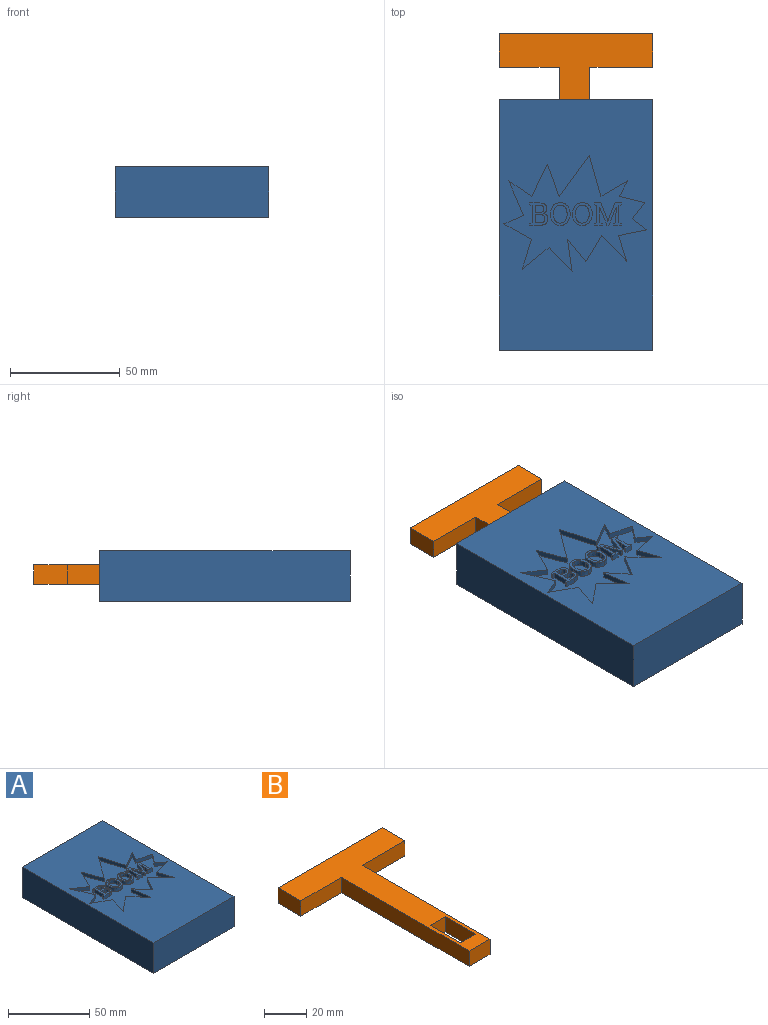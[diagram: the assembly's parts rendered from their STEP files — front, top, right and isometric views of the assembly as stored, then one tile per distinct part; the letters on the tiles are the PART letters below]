
ASSEMBLY  parts=2 mates=1
PART A: 160 faces, bbox 69.9x114.3x22.9 mm
  f0: plane 114.3x69.85mm, normal (0,0,1), area 6341.6mm2, adj f18,f19,f20,f23,f91,f92,f93,f94
  f1: plane 25.4x15.24mm, normal (0,0,1), area 316mm2, adj f3,f4,f5,f9,f10,f11,f12,f24
  f2: plane 25.4x15.24mm, normal (0,0,1), area 316mm2, adj f6,f7,f8,f14,f15,f16,f17,f21
  f3: plane 5.08x4.78mm, normal (0,-1,0), area 24.3mm2, adj f1,f4,f24,f25
  f4: plane 5.08x5.08mm, normal (-1,0,0), area 25.8mm2, adj f1,f3,f5,f25
  f5: cylinder r=3.97mm len=7.94mm, axis (0,0,-1), area 100.6mm2, adj f1,f4,f24,f25
  f6: plane 5.08x5.08mm, normal (-1,0,0), area 25.8mm2, adj f2,f7,f21,f25
  f7: cylinder r=3.97mm len=7.94mm, axis (0,0,-1), area 100.6mm2, adj f2,f6,f8,f25
  f8: plane 5.08x5.08mm, normal (1,0,0), area 25.8mm2, adj f2,f7,f21,f25
  f9: plane 25.4x5.08mm, normal (-1,0,0), area 129mm2, adj f1,f10,f12,f25
  f10: plane 15.24x5.08mm, normal (0,-1,0), area 77.4mm2, adj f1,f9,f11,f25
  f11: plane 25.4x5.08mm, normal (1,0,0), area 129mm2, adj f1,f10,f12,f25
  f12: plane 49.53x17.78mm, normal (0,-1,0), area 648.4mm2, adj f1,f9,f11,f13,f22,f25,f26,f27
  f13: plane 93.98x17.78mm, normal (-1,0,0), area 1671mm2, adj f12,f17,f25,f26
  f14: plane 25.4x5.08mm, normal (1,0,0), area 129mm2, adj f2,f15,f17,f25
  f15: plane 15.24x5.08mm, normal (0,1,0), area 77.4mm2, adj f2,f14,f16,f25
  f16: plane 25.4x5.08mm, normal (-1,0,0), area 129mm2, adj f2,f15,f17,f25
  f17: plane 49.53x17.78mm, normal (0,1,0), area 803.2mm2, adj f2,f13,f14,f16,f22,f25,f26
  f18: plane 114.3x22.86mm, normal (-1,0,0), area 2612.9mm2, adj f0,f19,f23,f25
  f19: plane 69.85x22.86mm, normal (0,-1,0), area 1596.8mm2, adj f0,f18,f20,f25
  f20: plane 114.3x22.86mm, normal (1,0,0), area 2612.9mm2, adj f0,f19,f23,f25
  f21: plane 5.08x4.78mm, normal (0,-1,0), area 24.3mm2, adj f2,f6,f8,f25
  f22: plane 93.98x17.78mm, normal (1,0,0), area 1671mm2, adj f12,f17,f25,f26
  f23: plane 69.85x22.86mm, normal (0,1,0), area 1441.9mm2, adj f0,f18,f20,f25,f26,f27,f28,f29
  f24: plane 5.08x5.08mm, normal (1,0,0), area 25.8mm2, adj f1,f3,f5,f25
  f25: plane 114.3x69.85mm, normal (0,0,-1), area 3960.9mm2, adj f3,f4,f5,f6,f7,f8,f9,f10
  f26: plane 104.14x49.53mm, normal (0,0,-1), area 4809.7mm2, adj f12,f13,f17,f22,f23,f27,f29
  f27: plane 10.16x10.16mm, normal (-1,0,0), area 103.2mm2, adj f12,f23,f26,f28
  f28: plane 15.24x10.16mm, normal (0,0,1), area 154.8mm2, adj f12,f23,f27,f29
  f29: plane 10.16x10.16mm, normal (1,0,0), area 103.2mm2, adj f12,f23,f26,f28
  f30: plane 2.94x2.54mm, normal (-1,0,0), area 7.5mm2, adj f31,f116,f117,f121
  f31: plane 4.11x2.54mm, normal (-1,0.03,0), area 10.4mm2, adj f30,f32,f117,f121
  f32: plane 2.54x0.04mm, normal (-0.18,-0.98,0), area 0.1mm2, adj f31,f33,f117,f121
  f33: plane 8.13x3.28mm, normal (0.93,-0.37,0), area 22.3mm2, adj f32,f34,f117,f121
  f34: plane 2.54x0.91mm, normal (0,-1,0), area 2.3mm2, adj f33,f35,f117,f121
  f35: plane 8.13x3.28mm, normal (-0.93,-0.37,0), area 22.3mm2, adj f34,f36,f117,f121
  f36: plane 2.54x0.04mm, normal (0.18,-0.98,0), area 0.1mm2, adj f35,f37,f117,f121
  f37: plane 4.11x2.54mm, normal (1,0.03,0), area 10.4mm2, adj f36,f38,f117,f121
  f38: plane 2.94x2.54mm, normal (1,0,0), area 7.5mm2, adj f37,f39,f117,f121
  f39: plane 2.54x1.14mm, normal (0.17,0.99,0), area 2.9mm2, adj f38,f40,f117,f121
  f40: plane 2.54x0.88mm, normal (1,0,0), area 2.2mm2, adj f39,f41,f117,f121
  f41: plane 3.64x2.54mm, normal (0,-1,0), area 9.3mm2, adj f40,f42,f117,f121
  f42: plane 2.54x0.88mm, normal (-1,0,0), area 2.2mm2, adj f41,f43,f117,f121
  f43: plane 2.54x1.14mm, normal (-0.17,0.99,0), area 2.9mm2, adj f42,f44,f117,f121
  f44: plane 7.99x2.54mm, normal (-1,0,0), area 20.3mm2, adj f43,f45,f117,f121
  f45: plane 2.54x1.14mm, normal (-0.17,-0.99,0), area 2.9mm2, adj f44,f46,f117,f121
  f46: plane 2.54x0.89mm, normal (-1,0,0), area 2.2mm2, adj f45,f47,f117,f121
  f47: plane 2.89x2.54mm, normal (0,1,0), area 7.3mm2, adj f46,f48,f117,f121
  f48: plane 8.24x3.23mm, normal (0.93,0.37,0), area 22.5mm2, adj f47,f49,f117,f121
  f49: plane 2.54x0.04mm, normal (0,1,0), area 0.1mm2, adj f48,f50,f117,f121
  f50: plane 8.24x3.22mm, normal (-0.93,0.36,0), area 22.5mm2, adj f49,f51,f117,f121
  f51: plane 2.9x2.54mm, normal (0,1,0), area 7.4mm2, adj f50,f52,f117,f121
  f52: plane 2.54x0.89mm, normal (1,0,0), area 2.2mm2, adj f51,f53,f117,f121
  f53: plane 2.54x1.14mm, normal (0.17,-0.99,0), area 2.9mm2, adj f52,f54,f117,f121
  f54: plane 7.99x2.54mm, normal (1,0,0), area 20.3mm2, adj f53,f55,f117,f121
  f55: plane 2.54x1.14mm, normal (0.17,0.99,0), area 2.9mm2, adj f54,f56,f117,f121
  f56: plane 2.54x0.88mm, normal (1,0,0), area 2.2mm2, adj f55,f57,f117,f121
  f57: plane 3.64x2.54mm, normal (0,-1,0), area 9.3mm2, adj f56,f58,f117,f121
  f58: plane 2.54x0.88mm, normal (-1,0,0), area 2.2mm2, adj f57,f116,f117,f121
  f59: extruded ~3.68x2.54mm, area 10.1mm2, adj f60,f112,f117,f120
  f60: plane 2.54x0.15mm, normal (1,0,0), area 0.4mm2, adj f59,f61,f117,f120
  f61: extruded ~3.68x2.54mm, area 10.1mm2, adj f60,f62,f117,f120
  f62: extruded ~3.29x2.54mm, area 9.5mm2, adj f61,f63,f117,f120
  f63: extruded ~3.19x2.54mm, area 9.2mm2, adj f62,f64,f117,f120
  f64: extruded ~3.68x2.54mm, area 10.1mm2, adj f63,f65,f117,f120
  f65: plane 2.54x0.15mm, normal (-1,0,0), area 0.4mm2, adj f64,f66,f117,f120
  f66: extruded ~3.68x2.54mm, area 10.1mm2, adj f65,f67,f117,f120
  f67: extruded ~3.19x2.54mm, area 9.2mm2, adj f66,f112,f117,f120
  f68: extruded ~3.68x2.54mm, area 10.1mm2, adj f69,f113,f117,f119
  f69: plane 2.54x0.15mm, normal (1,0,0), area 0.4mm2, adj f68,f70,f117,f119
  f70: extruded ~3.68x2.54mm, area 10.1mm2, adj f69,f71,f117,f119
  f71: extruded ~3.29x2.54mm, area 9.5mm2, adj f70,f72,f117,f119
  f72: extruded ~3.19x2.54mm, area 9.2mm2, adj f71,f73,f117,f119
  f73: extruded ~3.68x2.54mm, area 10.1mm2, adj f72,f74,f117,f119
  f74: plane 2.54x0.15mm, normal (-1,0,0), area 0.4mm2, adj f73,f75,f117,f119
  f75: extruded ~3.68x2.54mm, area 10.1mm2, adj f74,f76,f117,f119
  f76: extruded ~3.19x2.54mm, area 9.2mm2, adj f75,f113,f117,f119
  f77: plane 4.45x2.54mm, normal (0,1,0), area 11.3mm2, adj f78,f114,f117,f118
  f78: extruded ~2.54x2.48mm, area 6.7mm2, adj f77,f79,f117,f118
  f79: extruded ~2.54x2.06mm, area 5.9mm2, adj f78,f80,f117,f118
  f80: extruded ~2.54x1.21mm, area 3.3mm2, adj f79,f81,f117,f118
  f81: extruded ~2.54x1.13mm, area 3.6mm2, adj f80,f82,f117,f118
  f82: extruded ~2.54x1.44mm, area 4.4mm2, adj f81,f83,f117,f118
  f83: extruded ~2.54x1.64mm, area 4.5mm2, adj f82,f84,f117,f118
  f84: extruded ~2.54x2.13mm, area 6.1mm2, adj f83,f85,f117,f118
  f85: extruded ~2.54x2.45mm, area 6.6mm2, adj f84,f86,f117,f118
  f86: plane 4.88x2.54mm, normal (0,-1,0), area 12.4mm2, adj f85,f87,f117,f118
  f87: plane 2.54x0.88mm, normal (-1,0,0), area 2.2mm2, adj f86,f88,f117,f118
  f88: plane 2.54x1.14mm, normal (-0.17,0.99,0), area 2.9mm2, adj f87,f89,f117,f118
  f89: plane 7.99x2.54mm, normal (-1,0,0), area 20.3mm2, adj f88,f90,f117,f118
  f90: plane 2.54x1.14mm, normal (-0.17,-0.99,0), area 2.9mm2, adj f89,f114,f117,f118
  f91: plane 11.08x10.5mm, normal (0.73,0.69,0), area 38.8mm2, adj f0,f92,f115,f117
  f92: plane 14.68x2.54mm, normal (-0.99,-0.14,0), area 37.7mm2, adj f0,f91,f93,f117
  f93: plane 10.09x8.4mm, normal (0.77,0.64,0), area 33.4mm2, adj f0,f92,f94,f117
  f94: plane 12.03x7.26mm, normal (-0.86,0.52,0), area 35.7mm2, adj f0,f93,f95,f117
  f95: plane 12.03x11.46mm, normal (0.72,0.69,0), area 42.2mm2, adj f0,f94,f96,f117
  f96: plane 11.84x3.82mm, normal (-0.95,-0.31,0), area 31.6mm2, adj f0,f95,f97,f117
  f97: plane 12.83x2.58mm, normal (-0.2,0.98,0), area 33.2mm2, adj f0,f96,f98,f117
  f98: plane 6.53x5.06mm, normal (-0.61,-0.79,0), area 21mm2, adj f0,f97,f99,f117
  f99: plane 7.4x5.73mm, normal (-0.79,0.61,0), area 23.8mm2, adj f0,f98,f100,f117
  f100: plane 11.65x2.92mm, normal (-0.24,-0.97,0), area 30.5mm2, adj f0,f99,f101,f117
  f101: plane 7.04x3.82mm, normal (-0.88,0.48,0), area 20.3mm2, adj f0,f100,f102,f117
  f102: plane 12.22x7.04mm, normal (0.5,-0.87,0), area 35.8mm2, adj f0,f101,f103,f117
  f103: plane 18.71x5.35mm, normal (-0.96,-0.27,0), area 49.4mm2, adj f0,f102,f104,f117
  f104: plane 18.71x13.75mm, normal (0.81,-0.59,0), area 59mm2, adj f0,f103,f105,f117
  f105: plane 14.51x5.35mm, normal (-0.94,-0.35,0), area 39.3mm2, adj f0,f104,f106,f117
  f106: plane 14.51x7.26mm, normal (0.89,-0.45,0), area 41.2mm2, adj f0,f105,f107,f117
  f107: plane 10.36x7.04mm, normal (-0.56,-0.83,0), area 31.8mm2, adj f0,f106,f108,f117
  f108: plane 15.82x6.73mm, normal (0.92,0.39,0), area 43.7mm2, adj f0,f107,f109,f117
  f109: plane 8.98x3.82mm, normal (0.39,-0.92,0), area 24.8mm2, adj f0,f108,f110,f117
  f110: plane 12.6x7.09mm, normal (0.49,0.87,0), area 36.7mm2, adj f0,f109,f111,f117
  f111: plane 13.53x4.2mm, normal (0.96,-0.3,0), area 36mm2, adj f0,f110,f115,f117
  f112: extruded ~3.29x2.54mm, area 9.5mm2, adj f59,f67,f117,f120
  f113: extruded ~3.29x2.54mm, area 9.5mm2, adj f68,f76,f117,f119
  f114: plane 2.54x0.89mm, normal (-1,0,0), area 2.2mm2, adj f77,f90,f117,f118
  f115: plane 12.22x9.93mm, normal (-0.63,0.78,0), area 40mm2, adj f0,f91,f111,f117
  f116: plane 2.54x1.14mm, normal (-0.17,0.99,0), area 2.9mm2, adj f30,f58,f117,f121
  f117: plane 65.15x53.09mm, normal (0,0,1), area 1369mm2, adj f30,f31,f32,f33,f34,f35,f36,f37
  f118: plane 10.15x8.24mm, normal (0,0,1), area 40.4mm2, adj f77,f78,f79,f80,f81,f82,f83,f84
  f119: plane 10.44x8.98mm, normal (0,0,1), area 33.7mm2, adj f68,f69,f70,f71,f72,f73,f74,f75
  f120: plane 10.44x8.98mm, normal (0,0,1), area 33.7mm2, adj f59,f60,f61,f62,f63,f64,f65,f66
  f121: plane 12.29x10.15mm, normal (0,0,1), area 55.8mm2, adj f30,f31,f32,f33,f34,f35,f36,f37
  f122: extruded ~2.91x2.54mm, area 7.8mm2, adj f120,f123,f131,f132
  f123: plane 2.54x0.16mm, normal (-1,0,0), area 0.4mm2, adj f120,f122,f124,f132
  f124: extruded ~2.89x2.54mm, area 7.8mm2, adj f120,f123,f125,f132
  f125: extruded ~2.54x2.34mm, area 6.9mm2, adj f120,f124,f126,f132
  f126: extruded ~2.54x2.24mm, area 6.6mm2, adj f120,f125,f127,f132
  f127: extruded ~2.88x2.54mm, area 7.7mm2, adj f120,f126,f128,f132
  f128: plane 2.54x0.16mm, normal (1,0,0), area 0.4mm2, adj f120,f127,f129,f132
  f129: extruded ~2.9x2.54mm, area 7.8mm2, adj f120,f128,f130,f132
  f130: extruded ~2.54x2.24mm, area 6.6mm2, adj f120,f129,f131,f132
  f131: extruded ~2.54x2.35mm, area 6.9mm2, adj f120,f122,f130,f132
  f132: plane 8.19x6.23mm, normal (0,0,1), area 41.6mm2, adj f122,f123,f124,f125,f126,f127,f128,f129
  f133: extruded ~2.91x2.54mm, area 7.8mm2, adj f119,f134,f142,f143
  f134: plane 2.54x0.16mm, normal (-1,0,0), area 0.4mm2, adj f119,f133,f135,f143
  f135: extruded ~2.89x2.54mm, area 7.8mm2, adj f119,f134,f136,f143
  f136: extruded ~2.54x2.34mm, area 6.9mm2, adj f119,f135,f137,f143
  f137: extruded ~2.54x2.24mm, area 6.6mm2, adj f119,f136,f138,f143
  f138: extruded ~2.88x2.54mm, area 7.7mm2, adj f119,f137,f139,f143
  f139: plane 2.54x0.16mm, normal (1,0,0), area 0.4mm2, adj f119,f138,f140,f143
  f140: extruded ~2.9x2.54mm, area 7.8mm2, adj f119,f139,f141,f143
  f141: extruded ~2.54x2.24mm, area 6.6mm2, adj f119,f140,f142,f143
  f142: extruded ~2.54x2.35mm, area 6.9mm2, adj f119,f133,f141,f143
  f143: plane 8.19x6.23mm, normal (0,0,1), area 41.6mm2, adj f133,f134,f135,f136,f137,f138,f139,f140
  f144: extruded ~2.54x1.33mm, area 3.7mm2, adj f118,f145,f150,f151
  f145: plane 2.58x2.54mm, normal (0,-1,0), area 6.5mm2, adj f118,f144,f146,f151
  f146: plane 3.69x2.54mm, normal (1,0,0), area 9.4mm2, adj f118,f145,f147,f151
  f147: plane 2.54x2.37mm, normal (0,1,0), area 6mm2, adj f118,f146,f148,f151
  f148: extruded ~2.54x1.46mm, area 4mm2, adj f118,f147,f149,f151
  f149: extruded ~2.54x1.31mm, area 3.7mm2, adj f118,f148,f150,f151
  f150: extruded ~2.54x1.4mm, area 3.8mm2, adj f118,f144,f149,f151
  f151: plane 4.35x3.69mm, normal (0,0,1), area 14.8mm2, adj f144,f145,f146,f147,f148,f149,f150
  f152: plane 2.54x1.94mm, normal (0,-1,0), area 4.9mm2, adj f118,f153,f158,f159
  f153: plane 3.23x2.54mm, normal (1,0,0), area 8.2mm2, adj f118,f152,f154,f159
  f154: plane 2.54x2.29mm, normal (0,1,0), area 5.8mm2, adj f118,f153,f155,f159
  f155: extruded ~2.54x1.2mm, area 3.3mm2, adj f118,f154,f156,f159
  f156: extruded ~2.54x1.16mm, area 3.3mm2, adj f118,f155,f157,f159
  f157: extruded ~2.54x1.23mm, area 3.5mm2, adj f118,f156,f158,f159
  f158: extruded ~2.54x1.49mm, area 4mm2, adj f118,f152,f157,f159
  f159: plane 3.94x3.23mm, normal (0,0,1), area 11.7mm2, adj f152,f153,f154,f155,f156,f157,f158
PART B: 14 faces, bbox 69.9x100.8x8.9 mm
  f0: plane 100.84x69.85mm, normal (0,0,-1), area 2053.9mm2, adj f1,f3,f4,f5,f6,f7,f8,f9
  f1: plane 85.6x8.89mm, normal (1,0,0), area 761mm2, adj f0,f2,f4,f9
  f2: plane 100.84x69.85mm, normal (0,0,1), area 2053.9mm2, adj f1,f3,f4,f5,f6,f7,f8,f9
  f3: plane 85.6x8.89mm, normal (-1,0,0), area 761mm2, adj f0,f2,f4,f13
  f4: plane 13.97x8.89mm, normal (0,-1,0), area 124.2mm2, adj f0,f1,f2,f3
  f5: plane 20.32x8.89mm, normal (-1,0,0), area 180.6mm2, adj f0,f2,f6,f8
  f6: plane 10.16x8.89mm, normal (0,-1,0), area 90.3mm2, adj f0,f2,f5,f7
  f7: plane 20.32x8.89mm, normal (1,0,0), area 180.6mm2, adj f0,f2,f6,f8
  f8: plane 10.16x8.89mm, normal (0,1,0), area 90.3mm2, adj f0,f2,f5,f7
  f9: plane 28.58x8.89mm, normal (0,-1,0), area 254mm2, adj f0,f1,f2,f11
  f10: plane 15.24x8.89mm, normal (-1,0,0), area 135.5mm2, adj f0,f2,f12,f13
  f11: plane 15.24x8.89mm, normal (1,0,0), area 135.5mm2, adj f0,f2,f9,f12
  f12: plane 69.85x8.89mm, normal (0,1,0), area 621mm2, adj f0,f2,f10,f11
  f13: plane 27.31x8.89mm, normal (0,-1,0), area 242.7mm2, adj f0,f2,f3,f10
PLACE A t=(-10.94,-3.34,-3.33)mm fixed
PLACE B t=(62.68,9.95,-7.36)mm
MATE slider A.f23 <-> B.f13  axis (0,1,0) through (-18.56,60.47,4.29)mm
